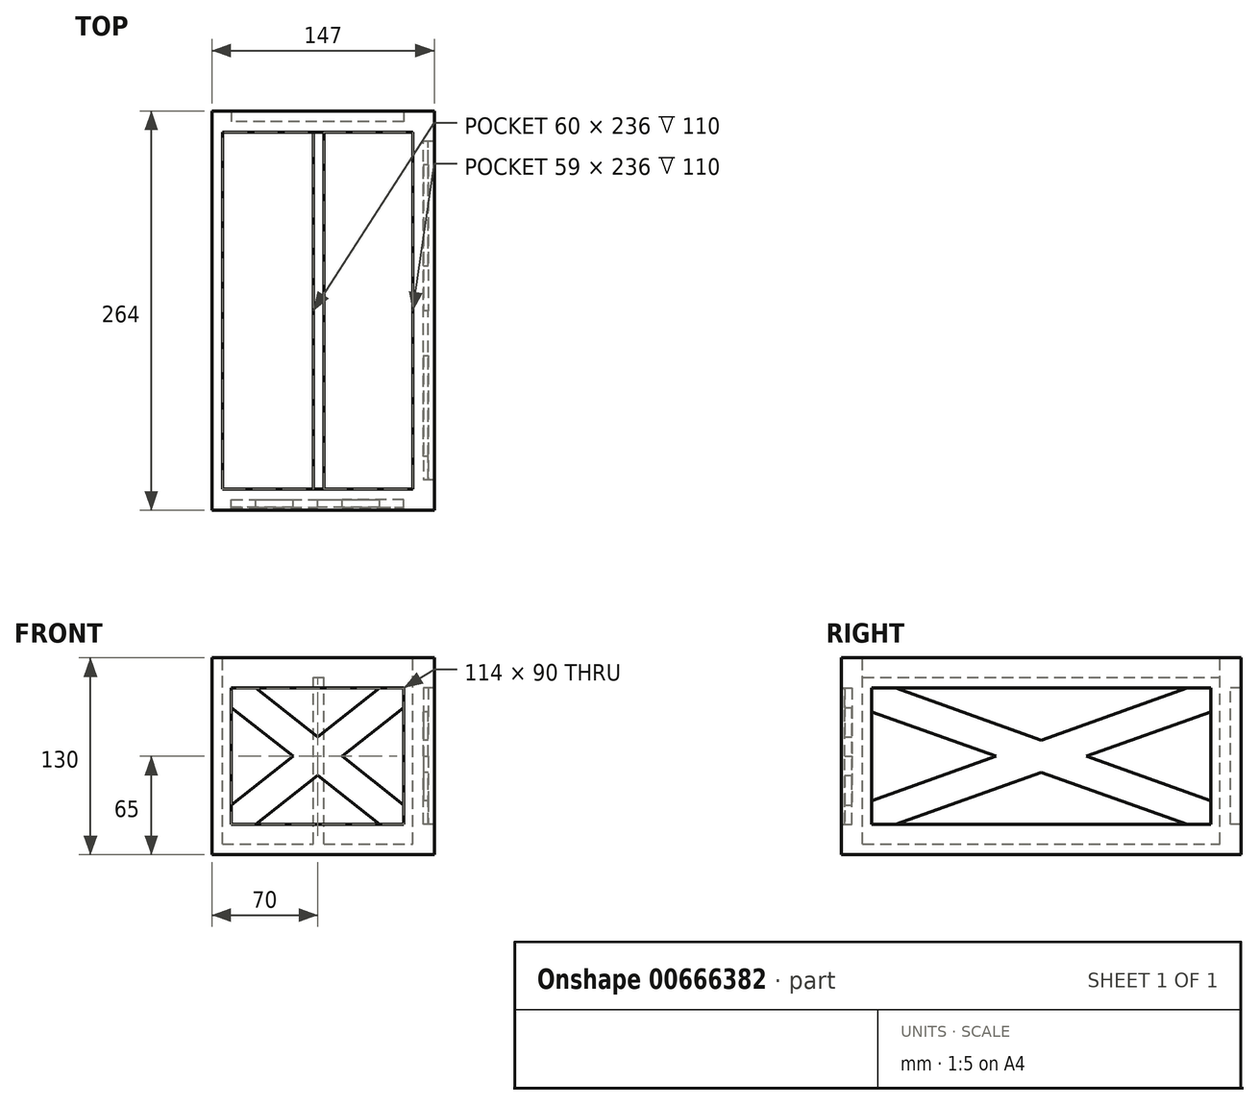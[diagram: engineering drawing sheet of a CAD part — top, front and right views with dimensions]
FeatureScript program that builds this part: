
annotation { "Feature Type Name" : "Feature", "Feature Type Description" : "" }
export const myFeature = defineFeature(function(context is Context, id is Id, definition is map)
    precondition{}
    {
        {
            var Q0;
            Q0=qCreatedBy(makeId("Front.planeOp"),FACE);
            var sketch = newSketch(context, id + "F0", { "sketchPlane" : qUnion([Q0])});
            skLineSegment(sketch, "E0.bottom", {"start": v(0, 0) * mm, "end": v(140, 0) * mm});
            skLineSegment(sketch, "E0.top", {"start": v(0, 130) * mm, "end": v(140, 130) * mm});
            skLineSegment(sketch, "E0.left", {"start": v(0, 0) * mm, "end": v(0, 130) * mm});
            skLineSegment(sketch, "E0.right", {"start": v(140, 0) * mm, "end": v(140, 130) * mm});
            skSolve(sketch);
        }
        {
            var Q0;
            Q0 = qSketchRegion(id + "F0", true);
            extrude(context, id + "F1", {"entities" : qUnion([Q0]), "depth" : 250 * mm, "offsetDistance" : 25 * mm});
        }
        {
            var Q0;
            Q0=makeQuery(id+"F1.opExtrude","SWEPT_FACE",FACE,{"disambiguationData":[OSD([sQuery(id+"F0.wireOp",EDGE,"E0.top")])]});
            var sketch = newSketch(context, id + "F2", { "sketchPlane" : qUnion([Q0])});
            skLineSegment(sketch, "E1.bottom", {"start": v(7, -7) * mm, "end": v(133, -7) * mm});
            skLineSegment(sketch, "E1.top", {"start": v(7, -243) * mm, "end": v(133, -243) * mm});
            skLineSegment(sketch, "E1.left", {"start": v(7, -7) * mm, "end": v(7, -243) * mm});
            skLineSegment(sketch, "E1.right", {"start": v(133, -7) * mm, "end": v(133, -243) * mm});
            skSolve(sketch);
        }
        {
            var Q0;
            Q0 = qSketchRegion(id + "F2", true);
            extrude(context, id + "F3", {"entities" : qUnion([Q0]), "operationType" : NewBodyOperationType.REMOVE, "oppositeDirection" : true, "depth" : 123 * mm, "offsetDistance" : 25 * mm});
        }
        {
            var Q0;
            Q0=makeQuery(id+"F1.opExtrude","SWEPT_FACE",FACE,{"disambiguationData":[OSD([sQuery(id+"F0.wireOp",EDGE,"E0.right")])]});
            var sketch = newSketch(context, id + "F4", { "sketchPlane" : qUnion([Q0])});
            skLineSegment(sketch, "E2.0", {"start": v(-250, 130) * mm, "end": v(0, 130) * mm});
            skLineSegment(sketch, "E3.0", {"start": v(-250, 0) * mm, "end": v(-250, 130) * mm});
            skLineSegment(sketch, "E4.0", {"start": v(-250, 0) * mm, "end": v(0, 0) * mm});
            skLineSegment(sketch, "E5.0", {"start": v(0, 0) * mm, "end": v(0, 130) * mm});
            skLineSegment(sketch, "E6.bottom", {"start": v(-237, 110) * mm, "end": v(-13, 110) * mm});
            skLineSegment(sketch, "E6.top", {"start": v(-237, 20) * mm, "end": v(-13, 20) * mm});
            skLineSegment(sketch, "E6.left", {"start": v(-237, 110) * mm, "end": v(-237, 20) * mm});
            skLineSegment(sketch, "E6.right", {"start": v(-13, 110) * mm, "end": v(-13, 20) * mm});
            skLineSegment(sketch, "E7.bottom", {"start": v(-250, 130) * mm, "end": v(-257, 130) * mm});
            skLineSegment(sketch, "E7.top", {"start": v(-250, 0) * mm, "end": v(-257, 0) * mm});
            skLineSegment(sketch, "E7.left", {"start": v(-250, 130) * mm, "end": v(-250, 0) * mm});
            skLineSegment(sketch, "E7.right", {"start": v(-257, 130) * mm, "end": v(-257, 0) * mm});
            skLineSegment(sketch, "E8.bottom", {"start": v(0, 0) * mm, "end": v(7, 0) * mm});
            skLineSegment(sketch, "E8.top", {"start": v(0, 130) * mm, "end": v(7, 130) * mm});
            skLineSegment(sketch, "E8.right", {"start": v(7, 0) * mm, "end": v(7, 130) * mm});
            skSolve(sketch);
        }
        {
            var Q0;
            Q0 = qSketchRegion(id + "F4", true);
            extrude(context, id + "F5", {"entities" : qUnion([Q0]), "operationType" : NewBodyOperationType.ADD, "depth" : 7 * mm, "offsetDistance" : 25 * mm});
        }
        {
            var Q0;
            Q0=qCreatedBy(makeId("Right.planeOp"),FACE);
            cPlane(context, id + "F6", {"entities" : qUnion([Q0]), "cplaneType" : CPlaneType.OFFSET, "offset" : 70 * mm, "width" : 150 * mm, "height" : 150 * mm});
        }
        {
            var Q0;
            Q0=makeQuery(id+"F1.opExtrude","CAP_FACE",FACE,{"disambiguationData":[OSD([sQuery(id+"F0.wireOp",EDGE,"E0.bottom"),sQuery(id+"F0.wireOp",EDGE,"E0.top"),sQuery(id+"F0.wireOp",EDGE,"E0.left"),sQuery(id+"F0.wireOp",EDGE,"E0.right")])],"isStart":false});
            var sketch = newSketch(context, id + "F7", { "sketchPlane" : qUnion([Q0])});
            skLineSegment(sketch, "E9.bottom", {"start": v(0, 0) * mm, "end": v(140, 0) * mm});
            skLineSegment(sketch, "E9.top", {"start": v(0, 130) * mm, "end": v(140, 130) * mm});
            skLineSegment(sketch, "E9.left", {"start": v(0, 0) * mm, "end": v(0, 130) * mm});
            skLineSegment(sketch, "E9.right", {"start": v(140, 0) * mm, "end": v(140, 130) * mm});
            skLineSegment(sketch, "E10.bottom", {"start": v(13, 20) * mm, "end": v(127, 20) * mm});
            skLineSegment(sketch, "E10.top", {"start": v(13, 110) * mm, "end": v(127, 110) * mm});
            skLineSegment(sketch, "E10.left", {"start": v(13, 20) * mm, "end": v(13, 110) * mm});
            skLineSegment(sketch, "E10.right", {"start": v(127, 20) * mm, "end": v(127, 110) * mm});
            skSolve(sketch);
        }
        {
            var Q0;
            Q0 = qSketchRegion(id + "F7", true);
            extrude(context, id + "F8", {"entities" : qUnion([Q0]), "operationType" : NewBodyOperationType.ADD, "depth" : 7 * mm, "offsetDistance" : 25 * mm});
        }
        {
            var Q0;
            Q0=makeQuery(id+"F1.opExtrude","CAP_FACE",FACE,{"disambiguationData":[OSD([sQuery(id+"F0.wireOp",EDGE,"E0.bottom"),sQuery(id+"F0.wireOp",EDGE,"E0.top"),sQuery(id+"F0.wireOp",EDGE,"E0.left"),sQuery(id+"F0.wireOp",EDGE,"E0.right")])],"isStart":true});
            var sketch = newSketch(context, id + "F9", { "sketchPlane" : qUnion([Q0])});
            skLineSegment(sketch, "E11.bottom", {"start": v(-140, 0) * mm, "end": v(0, 0) * mm});
            skLineSegment(sketch, "E11.top", {"start": v(-140, 130) * mm, "end": v(0, 130) * mm});
            skLineSegment(sketch, "E11.left", {"start": v(-140, 0) * mm, "end": v(-140, 130) * mm});
            skLineSegment(sketch, "E11.right", {"start": v(0, 0) * mm, "end": v(0, 130) * mm});
            skLineSegment(sketch, "E12.bottom", {"start": v(-127, 20) * mm, "end": v(-13, 20) * mm});
            skLineSegment(sketch, "E12.top", {"start": v(-127, 110) * mm, "end": v(-13, 110) * mm});
            skLineSegment(sketch, "E12.left", {"start": v(-127, 20) * mm, "end": v(-127, 110) * mm});
            skLineSegment(sketch, "E12.right", {"start": v(-13, 20) * mm, "end": v(-13, 110) * mm});
            skSolve(sketch);
        }
        {
            var Q0;
            Q0 = qSketchRegion(id + "F9", true);
            extrude(context, id + "F10", {"entities" : qUnion([Q0]), "operationType" : NewBodyOperationType.ADD, "depth" : 7 * mm, "offsetDistance" : 25 * mm});
        }
        {
            var Q0;
            Q0=makeQuery(id+"F1.opExtrude","SWEPT_FACE",FACE,{"disambiguationData":[OSD([sQuery(id+"F0.wireOp",EDGE,"E0.right")])]});
            var sketch = newSketch(context, id + "F11", { "sketchPlane" : qUnion([Q0])});
            skLineSegment(sketch, "E13", {"start": v(-221.35, 110) * mm, "end": v(-13, 35.65) * mm});
            skLineSegment(sketch, "E14", {"start": v(-13, 35.65) * mm, "end": v(-13, 20) * mm});
            skLineSegment(sketch, "E15", {"start": v(-13, 20) * mm, "end": v(-28.65, 20) * mm});
            skLineSegment(sketch, "E16", {"start": v(-28.65, 20) * mm, "end": v(-237, 94.35) * mm});
            skLineSegment(sketch, "E17", {"start": v(-237, 94.35) * mm, "end": v(-237, 110) * mm});
            skLineSegment(sketch, "E18", {"start": v(-237, 110) * mm, "end": v(-221.35, 110) * mm});
            skSolve(sketch);
        }
        {
            var Q0;
            Q0 = qSketchRegion(id + "F11", true);
            extrude(context, id + "F12", {"entities" : qUnion([Q0]), "operationType" : NewBodyOperationType.ADD, "depth" : 3 * mm, "offsetDistance" : 25 * mm});
        }
        {
            var Q0;
            Q0=makeQuery(id+"F12.boolean.opBoolean","SPLIT",FACE,{"disambiguationData":[TD([makeQuery(id+"F5.opExtrude","SWEPT_FACE",FACE,{"disambiguationData":[OSD([sQuery(id+"F4.wireOp",EDGE,"E6.bottom")])]})])],"derivedFrom":makeQuery(id+"F1.opExtrude","SWEPT_FACE",FACE,{"disambiguationData":[OSD([sQuery(id+"F0.wireOp",EDGE,"E0.right")])]})});
            var sketch = newSketch(context, id + "F13", { "sketchPlane" : qUnion([Q0])});
            skLineSegment(sketch, "E19", {"start": v(-28.65, 110) * mm, "end": v(-13, 110) * mm});
            skLineSegment(sketch, "E20", {"start": v(-13, 110) * mm, "end": v(-13, 94.35) * mm});
            skLineSegment(sketch, "E21", {"start": v(-237, 35.65) * mm, "end": v(-237, 20) * mm});
            skLineSegment(sketch, "E22", {"start": v(-237, 20) * mm, "end": v(-221.35, 20) * mm});
            skLineSegment(sketch, "E23", {"start": v(-221.35, 20) * mm, "end": v(-13, 94.35) * mm});
            skLineSegment(sketch, "E24", {"start": v(-28.65, 110) * mm, "end": v(-237, 35.65) * mm});
            skSolve(sketch);
        }
        {
            var Q0;
            Q0 = qSketchRegion(id + "F13", true);
            extrude(context, id + "F14", {"entities" : qUnion([Q0]), "operationType" : NewBodyOperationType.ADD, "depth" : 3 * mm, "offsetDistance" : 25 * mm});
        }
        {
            var Q0;
            Q0=makeQuery(id+"F3.boolean.opBoolean","COPY",FACE,{"derivedFrom":makeQuery(id+"F3.opExtrude","SWEPT_FACE",FACE,{"disambiguationData":[OSD([sQuery(id+"F2.wireOp",EDGE,"E1.bottom")])]})});
            var sketch = newSketch(context, id + "F15", { "sketchPlane" : qUnion([Q0])});
            skLineSegment(sketch, "E25.bottom", {"start": v(67, 7) * mm, "end": v(74, 7) * mm});
            skLineSegment(sketch, "E25.top", {"start": v(67, 117) * mm, "end": v(74, 117) * mm});
            skLineSegment(sketch, "E25.left", {"start": v(67, 7) * mm, "end": v(67, 117) * mm});
            skLineSegment(sketch, "E25.right", {"start": v(74, 7) * mm, "end": v(74, 117) * mm});
            skSolve(sketch);
        }
        {
            var Q0;
            Q0=makeQuery(id+"F15.imprint","IMPRINT",FACE,{"disambiguationData":[TD([[makeQuery(id+"F15.imprint","IMPRINT",EDGE,{"derivedFrom":sQuery(id+"F15.wireOp",EDGE,"E25.bottom")}),1.0]])]});
            extrude(context, id + "F16", {"entities" : qUnion([Q0]), "operationType" : NewBodyOperationType.ADD, "endBound" : BoundingType.UP_TO_NEXT, "depth" : 25 * mm, "offsetDistance" : 25 * mm});
        }
        {
            var Q0;
            Q0=makeQuery(id+"F1.opExtrude","CAP_FACE",FACE,{"disambiguationData":[OSD([sQuery(id+"F0.wireOp",EDGE,"E0.bottom"),sQuery(id+"F0.wireOp",EDGE,"E0.top"),sQuery(id+"F0.wireOp",EDGE,"E0.left"),sQuery(id+"F0.wireOp",EDGE,"E0.right")])],"isStart":false});
            var sketch = newSketch(context, id + "F17", { "sketchPlane" : qUnion([Q0])});
            skLineSegment(sketch, "E26", {"start": v(13, 110) * mm, "end": v(127, 20) * mm, "construction": true});
            skLineSegment(sketch, "E27", {"start": v(127, 110) * mm, "end": v(13, 20) * mm, "construction": true});
            skLineSegment(sketch, "E28", {"start": v(29.14, 110) * mm, "end": v(70, 77.74) * mm});
            skLineSegment(sketch, "E29", {"start": v(70, 77.74) * mm, "end": v(110.86, 110) * mm});
            skLineSegment(sketch, "E30", {"start": v(127, 97.26) * mm, "end": v(86.14, 65) * mm});
            skLineSegment(sketch, "E31", {"start": v(86.14, 65) * mm, "end": v(127, 32.74) * mm});
            skLineSegment(sketch, "E32", {"start": v(127, 32.74) * mm, "end": v(127, 20) * mm});
            skLineSegment(sketch, "E33", {"start": v(110.86, 20) * mm, "end": v(70, 52.26) * mm});
            skLineSegment(sketch, "E34", {"start": v(70, 52.26) * mm, "end": v(29.14, 20) * mm});
            skLineSegment(sketch, "E35", {"start": v(29.14, 20) * mm, "end": v(13, 20) * mm});
            skLineSegment(sketch, "E36", {"start": v(13, 32.74) * mm, "end": v(53.86, 65) * mm});
            skLineSegment(sketch, "E37", {"start": v(53.86, 65) * mm, "end": v(13, 97.26) * mm});
            skLineSegment(sketch, "E38", {"start": v(13, 97.26) * mm, "end": v(13, 110) * mm});
            skLineSegment(sketch, "E39", {"start": v(13, 110) * mm, "end": v(29.14, 110) * mm});
            skLineSegment(sketch, "E40", {"start": v(127, 110) * mm, "end": v(127, 97.26) * mm});
            skLineSegment(sketch, "E41", {"start": v(110.86, 110) * mm, "end": v(127, 110) * mm});
            skSolve(sketch);
        }
        {
            var Q0;
            Q0 = qSketchRegion(id + "F17", true);
            var Q1;
            Q1=makeQuery(id+"F17.imprint","IMPRINT",FACE,{"disambiguationData":[TD([[makeQuery(id+"F17.imprint","IMPRINT",EDGE,{"derivedFrom":sQuery(id+"F17.wireOp",EDGE,"E28")}),-1.0]])]});
            extrude(context, id + "F18", {"entities" : qUnion([Q0, Q1]), "operationType" : NewBodyOperationType.ADD, "depth" : 5 * mm, "offsetDistance" : 25 * mm});
        }
        {
            var Q0;
            Q0=qCreatedBy(makeId("Front.planeOp"),FACE);
            cPlane(context, id + "F19", {"entities" : qUnion([Q0]), "cplaneType" : CPlaneType.OFFSET, "offset" : 125 * mm, "width" : 150 * mm, "height" : 150 * mm});
        }
    });
